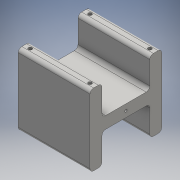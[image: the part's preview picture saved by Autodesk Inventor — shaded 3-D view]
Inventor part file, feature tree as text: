
AUTODESK INVENTOR PART (.ipt)
format: ipt  version: 2016 (Build 200138000, 138)  size: 157,184 bytes
history: native  units: mm
features: extrude x3, sketch x3, fillet x1
ambient origin geometry x8: Origin, YZ Plane, XZ Plane, XY Plane, X Axis, Y Axis, Z Axis, Center Point
bodies: Solid1 (feature_tree)
feature tree (7):
  extrude  "Block"  Depth=60.0mm
  extrude  "Motor Mount"  Depth=5.0mm
  extrude  "Plastic Savings"  Depth=3.0mm
  fillet  "Fillets FTW"  Radius=5.0mm
  sketch  "Sketch1"  dims[d0=60.0mm d1=60.0mm]
  sketch  "Sketch2"  dims[d2=5.0mm d3=5.0mm]
  sketch  "Sketch3"  dims[d4=5.0mm d5=5.0mm d6=5.0mm d7=5.0mm d8=5.0mm d9=5.0mm d10=3.0mm d11=3.0mm d12=3.0mm d13=3.0mm d14=60.0mm d15=0.0mm d17=2.0mm d18=60.0mm d19=0.0mm d20=10.0mm d21=10.0mm d22=5.0mm d23=5.0mm d24=60.0mm d25=0.0mm d26=3.0mm]
